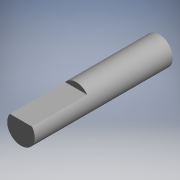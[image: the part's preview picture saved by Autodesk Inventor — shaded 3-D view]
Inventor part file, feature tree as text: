
AUTODESK INVENTOR PART (.ipt)
format: ipt  version: 2019.4 (Build 234330000, 330)  size: 96,768 bytes
history: native  units: mm
features: extrude x2, sketch x1
ambient origin geometry x8: Origin, YZ Plane, XZ Plane, XY Plane, X Axis, Y Axis, Z Axis, Center Point
bodies: Solid1 (feature_tree)
feature tree (3):
  sketch  "Sketch1"  dims[d0=5.0mm d1=4.0mm d2=10.0mm d3=0.0mm d4=15.0mm d5=0.0mm]
  extrude  "Extrusion1"  Depth=15.0mm
  extrude  "Extrusion2"  Depth=10.0mm TaperAngle=0.0deg
